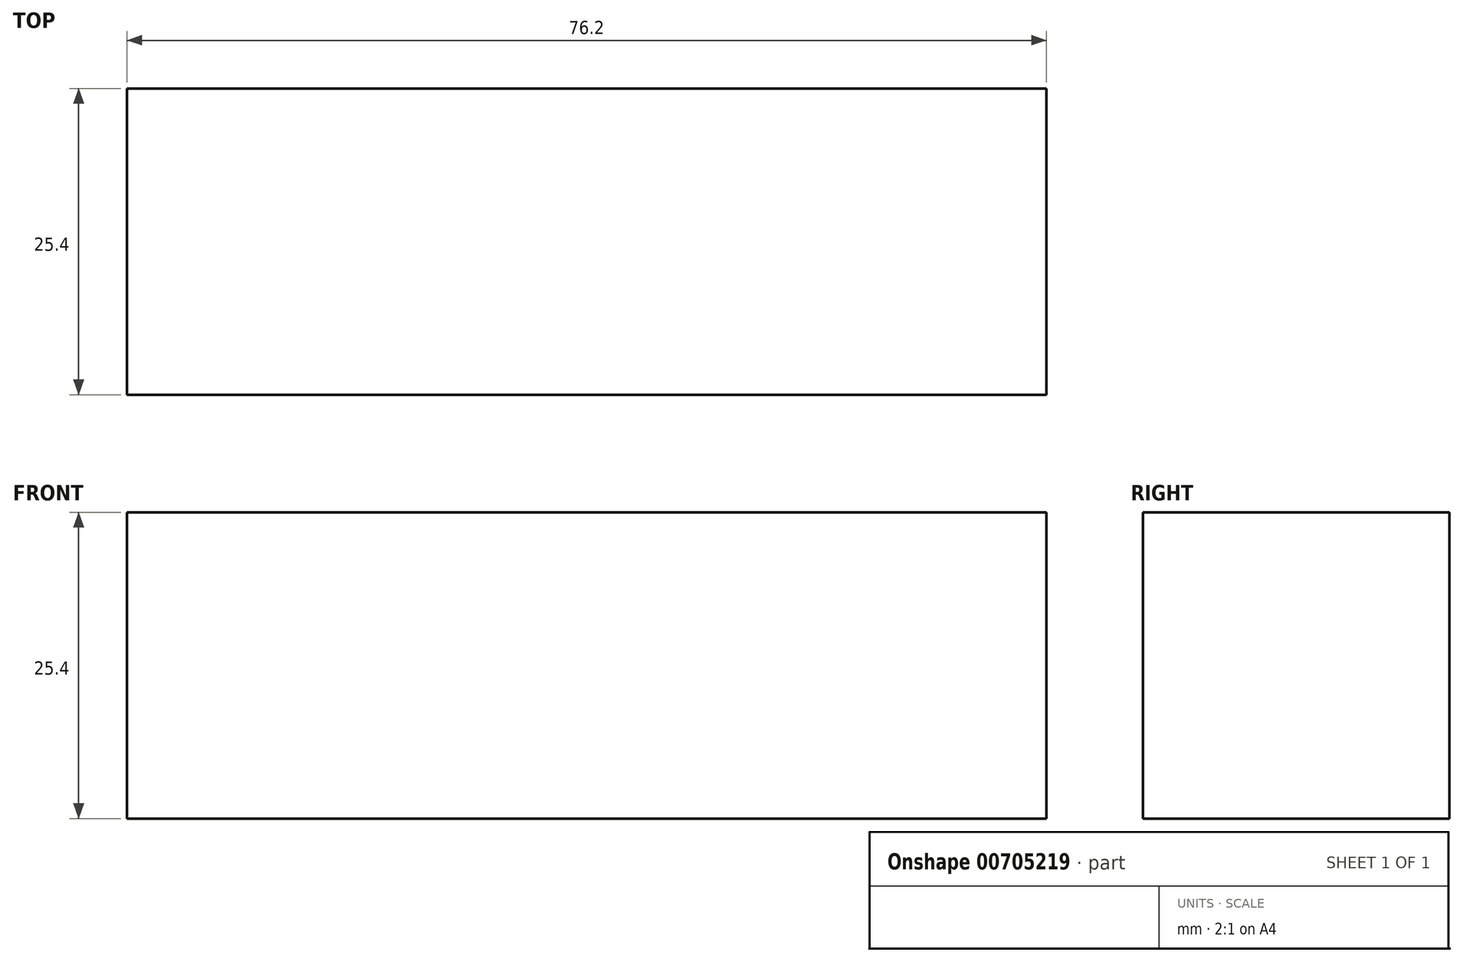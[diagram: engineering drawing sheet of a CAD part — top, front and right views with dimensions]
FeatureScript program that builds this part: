
annotation { "Feature Type Name" : "Feature", "Feature Type Description" : "" }
export const myFeature = defineFeature(function(context is Context, id is Id, definition is map)
    precondition{}
    {
        {
            var Q0;
            Q0=qCreatedBy(makeId("Front.planeOp"),FACE);
            var sketch = newSketch(context, id + "F0", { "sketchPlane" : qUnion([Q0])});
            skLineSegment(sketch, "E0.bottom", {"start": v(0, 0) * mm, "end": v(25.4, 0) * mm});
            skLineSegment(sketch, "E0.top", {"start": v(0, 25.4) * mm, "end": v(25.4, 25.4) * mm});
            skLineSegment(sketch, "E0.left", {"start": v(0, 0) * mm, "end": v(0, 25.4) * mm});
            skLineSegment(sketch, "E0.right", {"start": v(25.4, 0) * mm, "end": v(25.4, 25.4) * mm});
            skLineSegment(sketch, "E1.bottom", {"start": v(0, 25.4) * mm, "end": v(-25.4, 25.4) * mm});
            skLineSegment(sketch, "E1.top", {"start": v(0, 0) * mm, "end": v(-25.4, 0) * mm});
            skLineSegment(sketch, "E1.left", {"start": v(0, 25.4) * mm, "end": v(0, 0) * mm});
            skLineSegment(sketch, "E1.right", {"start": v(-25.4, 25.4) * mm, "end": v(-25.4, 0) * mm});
            skLineSegment(sketch, "E2.bottom", {"start": v(-25.4, 25.4) * mm, "end": v(-50.8, 25.4) * mm});
            skLineSegment(sketch, "E2.top", {"start": v(-25.4, 0) * mm, "end": v(-50.8, 0) * mm});
            skLineSegment(sketch, "E2.right", {"start": v(-50.8, 25.4) * mm, "end": v(-50.8, 0) * mm});
            skPoint(sketch, "E3.oppositeSnap0", {"position": v(0, 12.7) * mm});
            skLineSegment(sketch, "E3.bottom", {"start": v(-25.4, 25.4) * mm, "end": v(0, 25.4) * mm});
            skLineSegment(sketch, "E3.top", {"start": v(-25.4, 50.8) * mm, "end": v(0, 50.8) * mm});
            skLineSegment(sketch, "E3.left", {"start": v(-25.4, 25.4) * mm, "end": v(-25.4, 50.8) * mm});
            skLineSegment(sketch, "E3.right", {"start": v(0, 25.4) * mm, "end": v(0, 50.8) * mm});
            skSolve(sketch);
        }
        {
            var Q0;
            Q0=makeQuery(id+"F0.imprint","IMPRINT",FACE,{"disambiguationData":[TD([[makeQuery(id+"F0.imprint","IMPRINT",EDGE,{"derivedFrom":sQuery(id+"F0.wireOp",EDGE,"E3.bottom")}),1.0]])]});
            var Q1;
            Q1=makeQuery(id+"F0.imprint","IMPRINT",FACE,{"disambiguationData":[TD([[makeQuery(id+"F0.imprint","IMPRINT",EDGE,{"derivedFrom":sQuery(id+"F0.wireOp",EDGE,"E2.bottom")}),1.0]])]});
            var Q2;
            Q2=makeQuery(id+"F0.imprint","IMPRINT",FACE,{"disambiguationData":[TD([[makeQuery(id+"F0.imprint","IMPRINT",EDGE,{"derivedFrom":sQuery(id+"F0.wireOp",EDGE,"E1.top")}),-1.0]])]});
            var Q3;
            Q3=makeQuery(id+"F0.imprint","IMPRINT",FACE,{"disambiguationData":[TD([[makeQuery(id+"F0.imprint","IMPRINT",EDGE,{"derivedFrom":sQuery(id+"F0.wireOp",EDGE,"E0.bottom")}),1.0]])]});
            extrude(context, id + "F1", {"entities" : qUnion([Q0, Q1, Q2, Q3]), "depth" : 25.4 * mm, "offsetDistance" : 25.4 * mm});
        }
    });
